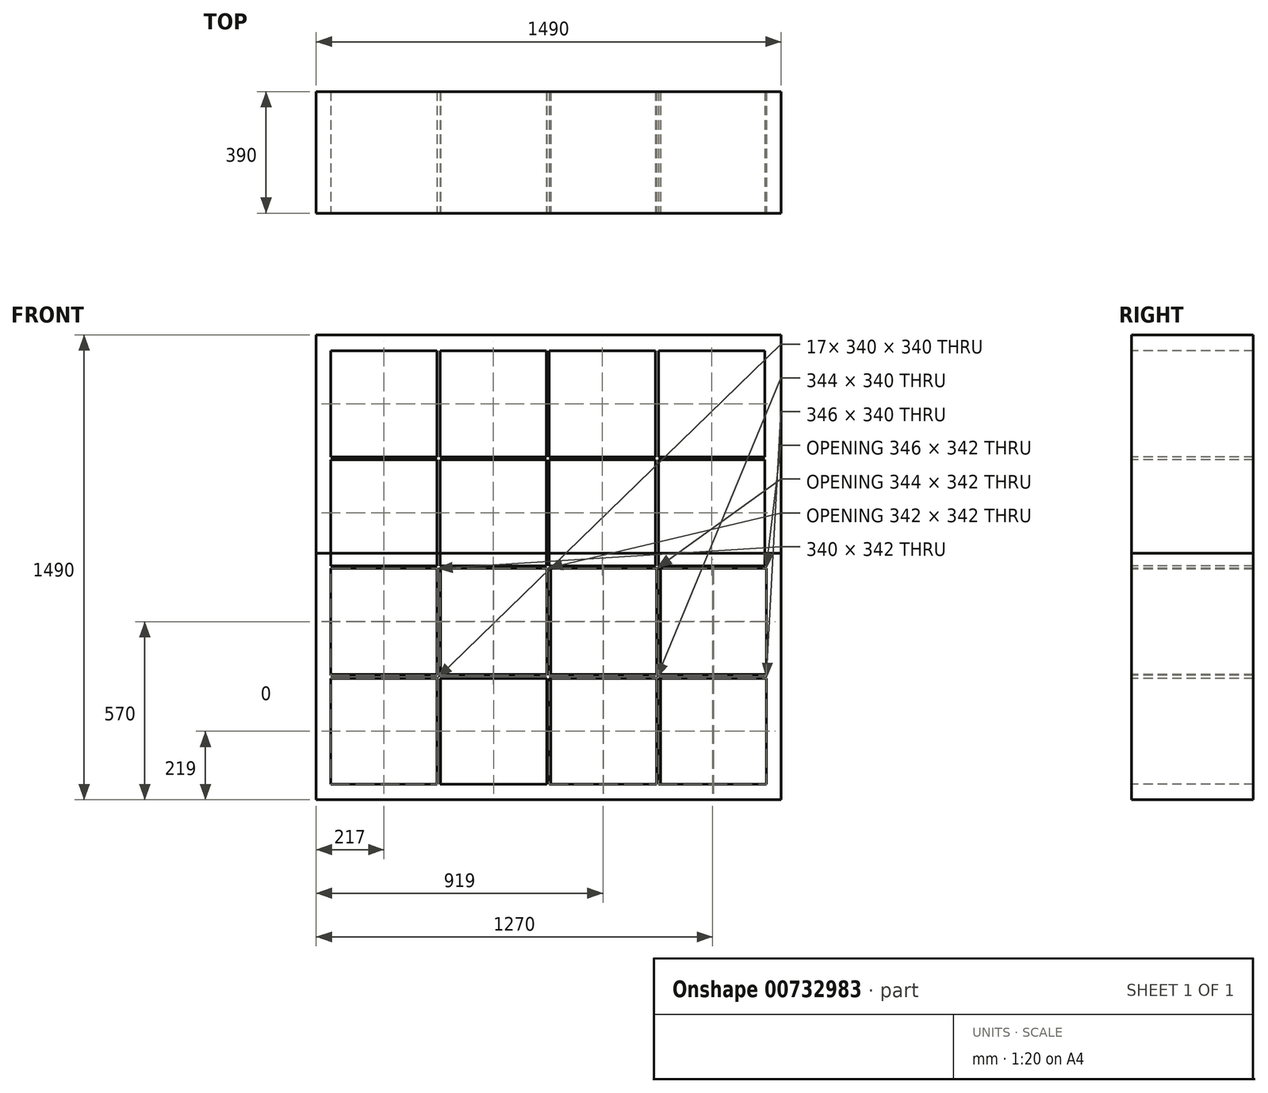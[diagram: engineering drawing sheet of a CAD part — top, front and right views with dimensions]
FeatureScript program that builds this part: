
annotation { "Feature Type Name" : "Feature", "Feature Type Description" : "" }
export const myFeature = defineFeature(function(context is Context, id is Id, definition is map)
    precondition{}
    {
        {
            var Q0;
            Q0=qCreatedBy(makeId("Top.planeOp"),FACE);
            var sketch = newSketch(context, id + "F0", { "sketchPlane" : qUnion([Q0])});
            skLineSegment(sketch, "E0.bottom", {"start": v(745, -195) * mm, "end": v(-745, -195) * mm});
            skLineSegment(sketch, "E0.top", {"start": v(745, 195) * mm, "end": v(-745, 195) * mm});
            skLineSegment(sketch, "E0.left", {"start": v(745, -195) * mm, "end": v(745, 195) * mm});
            skLineSegment(sketch, "E0.right", {"start": v(-745, -195) * mm, "end": v(-745, 195) * mm});
            skPoint(sketch, "E0.middle", {"position": v(0, 0) * mm});
            skSolve(sketch);
        }
        {
            var Q0;
            Q0=qSketchRegion(id+"F0",true);
            extrude(context, id + "F1", {"entities" : qUnion([Q0]), "depth" : 49 * mm});
        }
        {
            var Q0;
            Q0=makeQuery(id+"F1.opExtrude","CAP_FACE",FACE,{"disambiguationData":[OSD([sQuery(id+"F0.wireOp",EDGE,"E0.bottom"),sQuery(id+"F0.wireOp",EDGE,"E0.top"),sQuery(id+"F0.wireOp",EDGE,"E0.left"),sQuery(id+"F0.wireOp",EDGE,"E0.right")])],"isStart":false});
            var sketch = newSketch(context, id + "F2", { "sketchPlane" : qUnion([Q0])});
            skLineSegment(sketch, "E1.bottom", {"start": v(-745, -195) * mm, "end": v(-698, -195) * mm});
            skLineSegment(sketch, "E1.top", {"start": v(-745, 195) * mm, "end": v(-698, 195) * mm});
            skLineSegment(sketch, "E1.left", {"start": v(-745, -195) * mm, "end": v(-745, 195) * mm});
            skLineSegment(sketch, "E1.right", {"start": v(-698, -195) * mm, "end": v(-698, 195) * mm});
            skLineSegment(sketch, "E2.bottom", {"start": v(745, -195) * mm, "end": v(698, -195) * mm});
            skLineSegment(sketch, "E2.top", {"start": v(745, 195) * mm, "end": v(698, 195) * mm});
            skLineSegment(sketch, "E2.left", {"start": v(745, -195) * mm, "end": v(745, 195) * mm});
            skLineSegment(sketch, "E2.right", {"start": v(698, -195) * mm, "end": v(698, 195) * mm});
            skLineSegment(sketch, "E3.bottom", {"start": v(358, -195) * mm, "end": v(346, -195) * mm});
            skLineSegment(sketch, "E3.top", {"start": v(358, 195) * mm, "end": v(346, 195) * mm});
            skLineSegment(sketch, "E3.left", {"start": v(358, -195) * mm, "end": v(358, 195) * mm});
            skLineSegment(sketch, "E3.right", {"start": v(346, -195) * mm, "end": v(346, 195) * mm});
            skLineSegment(sketch, "E4.bottom", {"start": v(6, -195) * mm, "end": v(-6, -195) * mm});
            skLineSegment(sketch, "E4.top", {"start": v(6, 195) * mm, "end": v(-6, 195) * mm});
            skLineSegment(sketch, "E4.left", {"start": v(6, -195) * mm, "end": v(6, 195) * mm});
            skLineSegment(sketch, "E4.right", {"start": v(-6, -195) * mm, "end": v(-6, 195) * mm});
            skLineSegment(sketch, "E5.bottom", {"start": v(-346, -195) * mm, "end": v(-358, -195) * mm});
            skLineSegment(sketch, "E5.top", {"start": v(-346, 195) * mm, "end": v(-358, 195) * mm});
            skLineSegment(sketch, "E5.left", {"start": v(-346, -195) * mm, "end": v(-346, 195) * mm});
            skLineSegment(sketch, "E5.right", {"start": v(-358, -195) * mm, "end": v(-358, 195) * mm});
            skSolve(sketch);
        }
        {
            var Q0;
            Q0=qSketchRegion(id+"F2",true);
            extrude(context, id + "F3", {"entities" : qUnion([Q0]), "operationType" : NewBodyOperationType.ADD, "depth" : 692 * mm});
        }
        {
            var Q0;
            Q0=makeQuery(id+"F3.opExtrude","CAP_FACE",FACE,{"disambiguationData":[OSD([sQuery(id+"F2.wireOp",EDGE,"E1.bottom"),sQuery(id+"F2.wireOp",EDGE,"E1.top"),sQuery(id+"F2.wireOp",EDGE,"E1.left"),sQuery(id+"F2.wireOp",EDGE,"E1.right")])],"isStart":false});
            var sketch = newSketch(context, id + "F4", { "sketchPlane" : qUnion([Q0])});
            skLineSegment(sketch, "E6.bottom", {"start": v(-745, -195) * mm, "end": v(745, -195) * mm});
            skLineSegment(sketch, "E6.top", {"start": v(-745, 195) * mm, "end": v(745, 195) * mm});
            skLineSegment(sketch, "E6.left", {"start": v(-745, -195) * mm, "end": v(-745, 195) * mm});
            skLineSegment(sketch, "E6.right", {"start": v(745, -195) * mm, "end": v(745, 195) * mm});
            skSolve(sketch);
        }
        {
            var Q0;
            Q0=qSketchRegion(id+"F4",true);
            extrude(context, id + "F5", {"entities" : qUnion([Q0]), "operationType" : NewBodyOperationType.ADD, "depth" : 49 * mm});
        }
        {
            var Q0;
            Q0=makeQuery(id+"F3.opExtrude","SWEPT_FACE",FACE,{"disambiguationData":[OSD([sQuery(id+"F2.wireOp",EDGE,"E2.right")])]});
            var sketch = newSketch(context, id + "F6", { "sketchPlane" : qUnion([Q0])});
            skLineSegment(sketch, "E7.bottom", {"start": v(-195, 401) * mm, "end": v(195, 401) * mm});
            skLineSegment(sketch, "E7.top", {"start": v(-195, 389) * mm, "end": v(195, 389) * mm});
            skLineSegment(sketch, "E7.left", {"start": v(-195, 401) * mm, "end": v(-195, 389) * mm});
            skLineSegment(sketch, "E7.right", {"start": v(195, 401) * mm, "end": v(195, 389) * mm});
            skSolve(sketch);
        }
        {
            var Q0;
            Q0=qSketchRegion(id+"F6",true);
            extrude(context, id + "F7", {"entities" : qUnion([Q0]), "operationType" : NewBodyOperationType.ADD, "depth" : 1410 * mm});
        }
        {
            var Q0;
            Q0=makeQuery(id+"F7.boolean.opBoolean","MERGE",FACE,{"derivedFrom":[makeQuery(id+"F5.boolean.opBoolean","MERGE",FACE,{"derivedFrom":[makeQuery(id+"F3.boolean.opBoolean","MERGE",FACE,{"derivedFrom":[makeQuery(id+"F1.opExtrude","SWEPT_FACE",FACE,{"disambiguationData":[OSD([sQuery(id+"F0.wireOp",EDGE,"E0.bottom")])]}),makeQuery(id+"F3.opExtrude","SWEPT_FACE",FACE,{"disambiguationData":[OSD([sQuery(id+"F2.wireOp",EDGE,"E1.bottom")])]}),makeQuery(id+"F3.opExtrude","SWEPT_FACE",FACE,{"disambiguationData":[OSD([sQuery(id+"F2.wireOp",EDGE,"E2.bottom")])]}),makeQuery(id+"F3.opExtrude","SWEPT_FACE",FACE,{"disambiguationData":[OSD([sQuery(id+"F2.wireOp",EDGE,"E3.bottom")])]}),makeQuery(id+"F3.opExtrude","SWEPT_FACE",FACE,{"disambiguationData":[OSD([sQuery(id+"F2.wireOp",EDGE,"E4.bottom")])]}),makeQuery(id+"F3.opExtrude","SWEPT_FACE",FACE,{"disambiguationData":[OSD([sQuery(id+"F2.wireOp",EDGE,"E5.bottom")])]})]}),makeQuery(id+"F5.opExtrude","SWEPT_FACE",FACE,{"disambiguationData":[OSD([sQuery(id+"F4.wireOp",EDGE,"E6.bottom")])]})]}),makeQuery(id+"F7.opExtrude","SWEPT_FACE",FACE,{"disambiguationData":[OSD([sQuery(id+"F6.wireOp",EDGE,"E7.right")])]})]});
            var sketch = newSketch(context, id + "F8", { "sketchPlane" : qUnion([Q0])});
            skLineSegment(sketch, "E8.bottom", {"start": v(-745, 0) * mm, "end": v(745, 0) * mm});
            skLineSegment(sketch, "E8.top", {"start": v(-745, 1490) * mm, "end": v(745, 1490) * mm});
            skLineSegment(sketch, "E8.left", {"start": v(-745, 0) * mm, "end": v(-745, 1490) * mm});
            skLineSegment(sketch, "E8.right", {"start": v(745, 0) * mm, "end": v(745, 1490) * mm});
            skLineSegment(sketch, "E9.bottom", {"start": v(-698, 49) * mm, "end": v(-358, 49) * mm});
            skLineSegment(sketch, "E9.top", {"start": v(-698, 389) * mm, "end": v(-358, 389) * mm});
            skLineSegment(sketch, "E9.left", {"start": v(-698, 49) * mm, "end": v(-698, 389) * mm});
            skLineSegment(sketch, "E9.right", {"start": v(-358, 49) * mm, "end": v(-358, 389) * mm});
            skLineSegment(sketch, "E10.0.1.0", {"start": v(-698, 399) * mm, "end": v(-358, 399) * mm});
            skLineSegment(sketch, "E10.0.1.1", {"start": v(-698, 739) * mm, "end": v(-358, 739) * mm});
            skLineSegment(sketch, "E10.0.1.2", {"start": v(-698, 399) * mm, "end": v(-698, 739) * mm});
            skLineSegment(sketch, "E10.0.1.3", {"start": v(-358, 399) * mm, "end": v(-358, 739) * mm});
            skLineSegment(sketch, "E10.0.2.0", {"start": v(-698, 749) * mm, "end": v(-358, 749) * mm});
            skLineSegment(sketch, "E10.0.2.1", {"start": v(-698, 1089) * mm, "end": v(-358, 1089) * mm});
            skLineSegment(sketch, "E10.0.2.2", {"start": v(-698, 749) * mm, "end": v(-698, 1089) * mm});
            skLineSegment(sketch, "E10.0.2.3", {"start": v(-358, 749) * mm, "end": v(-358, 1089) * mm});
            skLineSegment(sketch, "E10.0.3.0", {"start": v(-698, 1099) * mm, "end": v(-358, 1099) * mm});
            skLineSegment(sketch, "E10.0.3.1", {"start": v(-698, 1439) * mm, "end": v(-358, 1439) * mm});
            skLineSegment(sketch, "E10.0.3.2", {"start": v(-698, 1099) * mm, "end": v(-698, 1439) * mm});
            skLineSegment(sketch, "E10.0.3.3", {"start": v(-358, 1099) * mm, "end": v(-358, 1439) * mm});
            skLineSegment(sketch, "E10.1.0.0", {"start": v(-348, 49) * mm, "end": v(-8, 49) * mm});
            skLineSegment(sketch, "E10.1.0.1", {"start": v(-348, 389) * mm, "end": v(-8, 389) * mm});
            skLineSegment(sketch, "E10.1.0.2", {"start": v(-348, 49) * mm, "end": v(-348, 389) * mm});
            skLineSegment(sketch, "E10.1.0.3", {"start": v(-8, 49) * mm, "end": v(-8, 389) * mm});
            skLineSegment(sketch, "E10.1.1.0", {"start": v(-348, 399) * mm, "end": v(-8, 399) * mm});
            skLineSegment(sketch, "E10.1.1.1", {"start": v(-348, 739) * mm, "end": v(-8, 739) * mm});
            skLineSegment(sketch, "E10.1.1.2", {"start": v(-348, 399) * mm, "end": v(-348, 739) * mm});
            skLineSegment(sketch, "E10.1.1.3", {"start": v(-8, 399) * mm, "end": v(-8, 739) * mm});
            skLineSegment(sketch, "E10.1.2.0", {"start": v(-348, 749) * mm, "end": v(-8, 749) * mm});
            skLineSegment(sketch, "E10.1.2.1", {"start": v(-348, 1089) * mm, "end": v(-8, 1089) * mm});
            skLineSegment(sketch, "E10.1.2.2", {"start": v(-348, 749) * mm, "end": v(-348, 1089) * mm});
            skLineSegment(sketch, "E10.1.2.3", {"start": v(-8, 749) * mm, "end": v(-8, 1089) * mm});
            skLineSegment(sketch, "E10.1.3.0", {"start": v(-348, 1099) * mm, "end": v(-8, 1099) * mm});
            skLineSegment(sketch, "E10.1.3.1", {"start": v(-348, 1439) * mm, "end": v(-8, 1439) * mm});
            skLineSegment(sketch, "E10.1.3.2", {"start": v(-348, 1099) * mm, "end": v(-348, 1439) * mm});
            skLineSegment(sketch, "E10.1.3.3", {"start": v(-8, 1099) * mm, "end": v(-8, 1439) * mm});
            skLineSegment(sketch, "E10.2.0.0", {"start": v(2, 49) * mm, "end": v(342, 49) * mm});
            skLineSegment(sketch, "E10.2.0.1", {"start": v(2, 389) * mm, "end": v(342, 389) * mm});
            skLineSegment(sketch, "E10.2.0.2", {"start": v(2, 49) * mm, "end": v(2, 389) * mm});
            skLineSegment(sketch, "E10.2.0.3", {"start": v(342, 49) * mm, "end": v(342, 389) * mm});
            skLineSegment(sketch, "E10.2.1.0", {"start": v(2, 399) * mm, "end": v(342, 399) * mm});
            skLineSegment(sketch, "E10.2.1.1", {"start": v(2, 739) * mm, "end": v(342, 739) * mm});
            skLineSegment(sketch, "E10.2.1.2", {"start": v(2, 399) * mm, "end": v(2, 739) * mm});
            skLineSegment(sketch, "E10.2.1.3", {"start": v(342, 399) * mm, "end": v(342, 739) * mm});
            skLineSegment(sketch, "E10.2.2.0", {"start": v(2, 749) * mm, "end": v(342, 749) * mm});
            skLineSegment(sketch, "E10.2.2.1", {"start": v(2, 1089) * mm, "end": v(342, 1089) * mm});
            skLineSegment(sketch, "E10.2.2.2", {"start": v(2, 749) * mm, "end": v(2, 1089) * mm});
            skLineSegment(sketch, "E10.2.2.3", {"start": v(342, 749) * mm, "end": v(342, 1089) * mm});
            skLineSegment(sketch, "E10.2.3.0", {"start": v(2, 1099) * mm, "end": v(342, 1099) * mm});
            skLineSegment(sketch, "E10.2.3.1", {"start": v(2, 1439) * mm, "end": v(342, 1439) * mm});
            skLineSegment(sketch, "E10.2.3.2", {"start": v(2, 1099) * mm, "end": v(2, 1439) * mm});
            skLineSegment(sketch, "E10.2.3.3", {"start": v(342, 1099) * mm, "end": v(342, 1439) * mm});
            skLineSegment(sketch, "E10.3.0.0", {"start": v(352, 49) * mm, "end": v(692, 49) * mm});
            skLineSegment(sketch, "E10.3.0.1", {"start": v(352, 389) * mm, "end": v(692, 389) * mm});
            skLineSegment(sketch, "E10.3.0.2", {"start": v(352, 49) * mm, "end": v(352, 389) * mm});
            skLineSegment(sketch, "E10.3.0.3", {"start": v(692, 49) * mm, "end": v(692, 389) * mm});
            skLineSegment(sketch, "E10.3.1.0", {"start": v(352, 399) * mm, "end": v(692, 399) * mm});
            skLineSegment(sketch, "E10.3.1.1", {"start": v(352, 739) * mm, "end": v(692, 739) * mm});
            skLineSegment(sketch, "E10.3.1.2", {"start": v(352, 399) * mm, "end": v(352, 739) * mm});
            skLineSegment(sketch, "E10.3.1.3", {"start": v(692, 399) * mm, "end": v(692, 739) * mm});
            skLineSegment(sketch, "E10.3.2.0", {"start": v(352, 749) * mm, "end": v(692, 749) * mm});
            skLineSegment(sketch, "E10.3.2.1", {"start": v(352, 1089) * mm, "end": v(692, 1089) * mm});
            skLineSegment(sketch, "E10.3.2.2", {"start": v(352, 749) * mm, "end": v(352, 1089) * mm});
            skLineSegment(sketch, "E10.3.2.3", {"start": v(692, 749) * mm, "end": v(692, 1089) * mm});
            skLineSegment(sketch, "E10.3.3.0", {"start": v(352, 1099) * mm, "end": v(692, 1099) * mm});
            skLineSegment(sketch, "E10.3.3.1", {"start": v(352, 1439) * mm, "end": v(692, 1439) * mm});
            skLineSegment(sketch, "E10.3.3.2", {"start": v(352, 1099) * mm, "end": v(352, 1439) * mm});
            skLineSegment(sketch, "E10.3.3.3", {"start": v(692, 1099) * mm, "end": v(692, 1439) * mm});
            skLineSegment(sketch, "E10.direction1", {"start": v(-698, 49) * mm, "end": v(-348, 49) * mm, "construction": true});
            skLineSegment(sketch, "E10.direction2", {"start": v(-698, 49) * mm, "end": v(-698, 399) * mm, "construction": true});
            skSolve(sketch);
        }
        {
            var Q0;
            {var subQ18=sQuery(id+"F8.wireOp",EDGE,"E8.top");Q0=makeQuery(id+"F8.imprint","IMPRINT",FACE,{"disambiguationData":[TD([[makeQuery(id+"F8.imprint","IMPRINT",EDGE,{"derivedFrom":subQ18}),-1.0]])]});}
            var Q1;
            {var subQ110=sQuery(id+"F8.wireOp",EDGE,"E8.bottom");Q1=makeQuery(id+"F8.imprint","IMPRINT",FACE,{"disambiguationData":[TD([[makeQuery(id+"F8.imprint","IMPRINT",EDGE,{"derivedFrom":subQ110}),-1.0]])]});}
            extrude(context, id + "F9", {"entities" : qUnion([Q0, Q1]), "oppositeDirection" : true, "depth" : 390 * mm, "offsetDistance" : 25 * mm});
        }
    });
